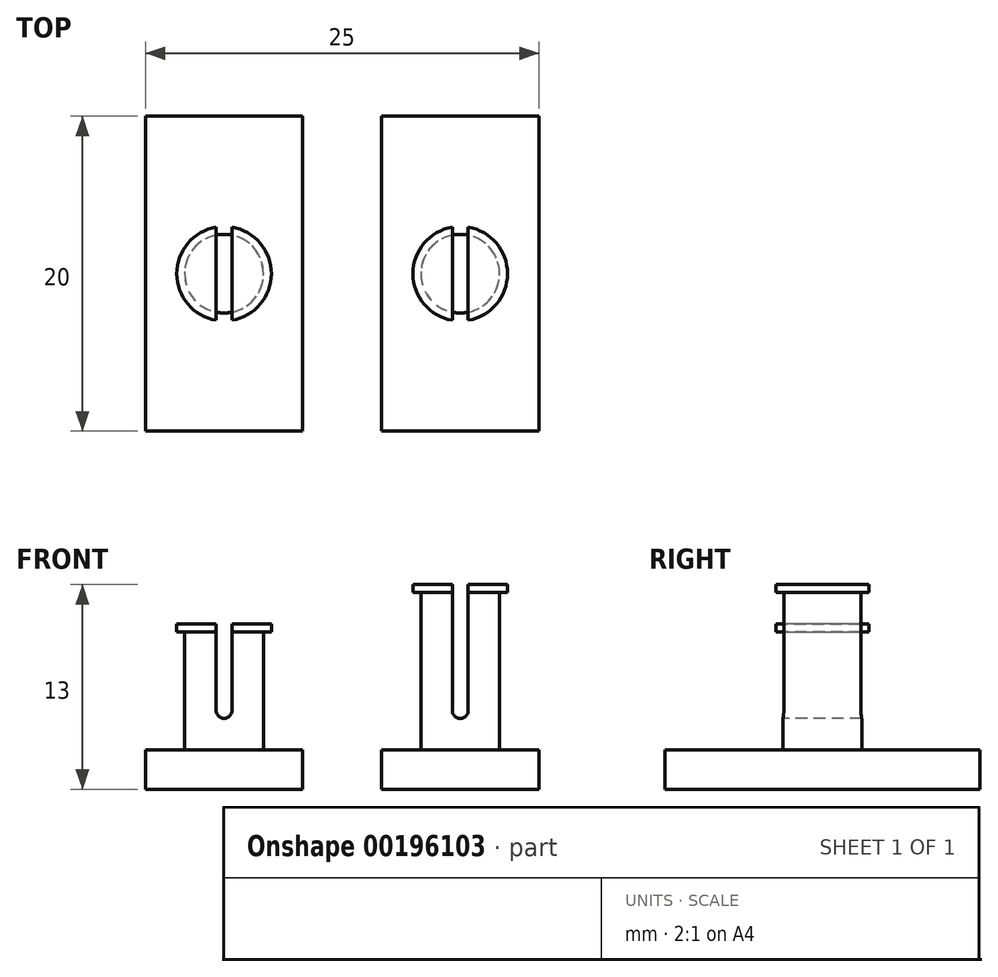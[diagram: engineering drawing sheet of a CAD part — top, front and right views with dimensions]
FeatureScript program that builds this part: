
annotation { "Feature Type Name" : "Feature", "Feature Type Description" : "" }
export const myFeature = defineFeature(function(context is Context, id is Id, definition is map)
    precondition{}
    {
        {
            var Q0;
            Q0=qCreatedBy(makeId("Front.planeOp"),FACE);
            var sketch = newSketch(context, id + "F0", { "sketchPlane" : qUnion([Q0])});
            skLineSegment(sketch, "E0", {"start": v(0, 0) * mm, "end": v(0, 16.22) * mm, "construction": true});
            skLineSegment(sketch, "E1", {"start": v(0, 8) * mm, "end": v(3, 8) * mm});
            skLineSegment(sketch, "E2", {"start": v(3, 8) * mm, "end": v(3, 7.5) * mm});
            skLineSegment(sketch, "E3", {"start": v(3, 7.5) * mm, "end": v(2.5, 7.5) * mm});
            skLineSegment(sketch, "E4", {"start": v(2.5, 7.5) * mm, "end": v(2.5, 2.5) * mm});
            skLineSegment(sketch, "E5", {"start": v(2.5, 2.5) * mm, "end": v(5, 2.5) * mm});
            skLineSegment(sketch, "E6", {"start": v(5, 2.5) * mm, "end": v(5, 0) * mm});
            skLineSegment(sketch, "E7", {"start": v(5, 0) * mm, "end": v(0, 0) * mm});
            skLineSegment(sketch, "E8", {"start": v(0, 8) * mm, "end": v(0, 0) * mm});
            skLineSegment(sketch, "E9", {"start": v(15, 0) * mm, "end": v(15, 15.04) * mm, "construction": true});
            skLineSegment(sketch, "E10", {"start": v(15, 10.5) * mm, "end": v(18, 10.5) * mm});
            skLineSegment(sketch, "E11", {"start": v(18, 10.5) * mm, "end": v(18, 10) * mm});
            skLineSegment(sketch, "E12", {"start": v(18, 10) * mm, "end": v(17.5, 10) * mm});
            skLineSegment(sketch, "E13", {"start": v(17.5, 10) * mm, "end": v(17.5, 2.5) * mm});
            skLineSegment(sketch, "E14", {"start": v(17.5, 2.5) * mm, "end": v(20, 2.5) * mm});
            skLineSegment(sketch, "E15", {"start": v(20, 2.5) * mm, "end": v(20, 0) * mm});
            skLineSegment(sketch, "E16", {"start": v(20, 0) * mm, "end": v(15, 0) * mm});
            skLineSegment(sketch, "E17", {"start": v(15, 10.5) * mm, "end": v(15, 0) * mm});
            skLineSegment(sketch, "E18", {"start": v(30, 0) * mm, "end": v(30, 27.9) * mm, "construction": true});
            skLineSegment(sketch, "E19", {"start": v(30, 13) * mm, "end": v(33, 13) * mm});
            skLineSegment(sketch, "E20", {"start": v(33, 13) * mm, "end": v(33, 12.5) * mm});
            skLineSegment(sketch, "E21", {"start": v(33, 12.5) * mm, "end": v(32.5, 12.5) * mm});
            skLineSegment(sketch, "E22", {"start": v(32.5, 12.5) * mm, "end": v(32.5, 2.5) * mm});
            skLineSegment(sketch, "E23", {"start": v(32.5, 2.5) * mm, "end": v(35, 2.5) * mm});
            skLineSegment(sketch, "E24", {"start": v(35, 2.5) * mm, "end": v(35, 0) * mm});
            skLineSegment(sketch, "E25", {"start": v(35, 0) * mm, "end": v(30, 0) * mm});
            skLineSegment(sketch, "E26", {"start": v(30, 13) * mm, "end": v(30, 0) * mm});
            skSolve(sketch);
        }
        {
            var Q0;
            Q0=makeQuery(id+"F0.imprint","IMPRINT",FACE,{"disambiguationData":[TD([[makeQuery(id+"F0.imprint","IMPRINT",EDGE,{"derivedFrom":sQuery(id+"F0.wireOp",EDGE,"E1")}),-1.0]])]});
            var Q1;
            Q1=sQuery(id+"F0.wireOp",EDGE,"E0");
            revolve(context, id + "F1", {"entities" : qUnion([Q0]), "axis" : qUnion([Q1]), "revolveType" : RevolveType.FULL});
        }
        {
            var Q0;
            Q0=makeQuery(id+"F0.imprint","IMPRINT",FACE,{"disambiguationData":[TD([[makeQuery(id+"F0.imprint","IMPRINT",EDGE,{"derivedFrom":sQuery(id+"F0.wireOp",EDGE,"E10")}),-1.0]])]});
            var Q1;
            Q1=sQuery(id+"F0.wireOp",EDGE,"E9");
            revolve(context, id + "F2", {"entities" : qUnion([Q0]), "axis" : qUnion([Q1]), "revolveType" : RevolveType.FULL});
        }
        {
            var Q0;
            Q0=makeQuery(id+"F0.imprint","IMPRINT",FACE,{"disambiguationData":[TD([[makeQuery(id+"F0.imprint","IMPRINT",EDGE,{"derivedFrom":sQuery(id+"F0.wireOp",EDGE,"E19")}),-1.0]])]});
            var Q1;
            Q1=sQuery(id+"F0.wireOp",EDGE,"E18");
            revolve(context, id + "F3", {"entities" : qUnion([Q0]), "axis" : qUnion([Q1]), "revolveType" : RevolveType.FULL});
        }
        {
            var Q0;
            Q0=qCreatedBy(makeId("Front.planeOp"),FACE);
            var sketch = newSketch(context, id + "F4", { "sketchPlane" : qUnion([Q0])});
            skLineSegment(sketch, "E27", {"start": v(0, 15.96) * mm, "end": v(0, 0) * mm, "construction": true});
            skLineSegment(sketch, "E28", {"start": v(0, 8) * mm, "end": v(0.5, 8) * mm});
            skLineSegment(sketch, "E29", {"start": v(0.5, 8) * mm, "end": v(0.5, 5) * mm});
            skLineSegment(sketch, "E30", {"start": v(0.5, 5) * mm, "end": v(0, 5) * mm, "construction": true});
            skLineSegment(sketch, "E31", {"start": v(0, 5) * mm, "end": v(0, 8) * mm});
            skArc(sketch, "E32", {"start": v(0, 4.5) * mm, "mid": v(0.35, 4.65) * mm, "end": v(0.5, 5) * mm});
            skLineSegment(sketch, "E33.MirrorCS", {"start": v(0, 8) * mm, "end": v(-0.5, 8) * mm});
            skLineSegment(sketch, "E34.MirrorCS", {"start": v(-0.5, 8) * mm, "end": v(-0.5, 5) * mm});
            skArc(sketch, "E35.MirrorCS", {"start": v(0, 4.5) * mm, "mid": v(-0.35, 4.65) * mm, "end": v(-0.5, 5) * mm});
            skLineSegment(sketch, "E36", {"start": v(15, 23.7) * mm, "end": v(15, 7.74) * mm, "construction": true});
            skLineSegment(sketch, "E37", {"start": v(15, 10.5) * mm, "end": v(15.5, 10.5) * mm});
            skLineSegment(sketch, "E38", {"start": v(15.5, 10.5) * mm, "end": v(15.5, 5) * mm});
            skLineSegment(sketch, "E39", {"start": v(15.5, 5) * mm, "end": v(15, 5) * mm, "construction": true});
            skLineSegment(sketch, "E40", {"start": v(15, 5) * mm, "end": v(15, 10.5) * mm});
            skArc(sketch, "E41", {"start": v(15, 4.5) * mm, "mid": v(15.35, 4.65) * mm, "end": v(15.5, 5) * mm});
            skLineSegment(sketch, "E42.MirrorCS", {"start": v(15, 10.5) * mm, "end": v(14.5, 10.5) * mm});
            skLineSegment(sketch, "E43.MirrorCS", {"start": v(14.5, 10.5) * mm, "end": v(14.5, 5) * mm});
            skArc(sketch, "E44.MirrorCS", {"start": v(15, 4.5) * mm, "mid": v(14.65, 4.65) * mm, "end": v(14.5, 5) * mm});
            skLineSegment(sketch, "E45", {"start": v(30, 24.52) * mm, "end": v(30, 8.56) * mm, "construction": true});
            skLineSegment(sketch, "E46", {"start": v(30, 13) * mm, "end": v(30.5, 13) * mm});
            skLineSegment(sketch, "E47", {"start": v(30.5, 13) * mm, "end": v(30.5, 5) * mm});
            skLineSegment(sketch, "E48", {"start": v(30.5, 5) * mm, "end": v(30, 5) * mm, "construction": true});
            skLineSegment(sketch, "E49", {"start": v(30, 5) * mm, "end": v(30, 13) * mm});
            skArc(sketch, "E50", {"start": v(30, 4.5) * mm, "mid": v(30.35, 4.65) * mm, "end": v(30.5, 5) * mm});
            skLineSegment(sketch, "E51.MirrorCS", {"start": v(30, 13) * mm, "end": v(29.5, 13) * mm});
            skLineSegment(sketch, "E52.MirrorCS", {"start": v(29.5, 13) * mm, "end": v(29.5, 5) * mm});
            skArc(sketch, "E53.MirrorCS", {"start": v(30, 4.5) * mm, "mid": v(29.65, 4.65) * mm, "end": v(29.5, 5) * mm});
            skSolve(sketch);
        }
        {
            var Q0;
            Q0=qSketchRegion(id+"F4",true);
            extrude(context, id + "F5", {"entities" : qUnion([Q0]), "operationType" : NewBodyOperationType.REMOVE, "oppositeDirection" : true, "depth" : 25 * mm, "hasSecondDirection" : true, "secondDirectionOppositeDirection" : false, "secondDirectionDepth" : 25 * mm});
        }
        {
            var Q0;
            Q0=makeQuery(id+"F1.opRevolve","SWEPT_FACE",FACE,{"disambiguationData":[OSD([sQuery(id+"F0.wireOp",EDGE,"E7")])]});
            var sketch = newSketch(context, id + "F6", { "sketchPlane" : qUnion([Q0])});
            skLineSegment(sketch, "E54.bottom", {"start": v(-5, 5) * mm, "end": v(5, 5) * mm});
            skLineSegment(sketch, "E54.top", {"start": v(-5, -5) * mm, "end": v(5, -5) * mm});
            skLineSegment(sketch, "E54.left", {"start": v(-5, 5) * mm, "end": v(-5, -5) * mm});
            skLineSegment(sketch, "E54.right", {"start": v(5, 5) * mm, "end": v(5, -5) * mm});
            skLineSegment(sketch, "E55.bottom", {"start": v(10, 10) * mm, "end": v(20, 10) * mm});
            skLineSegment(sketch, "E55.top", {"start": v(10, -10) * mm, "end": v(20, -10) * mm});
            skLineSegment(sketch, "E55.left", {"start": v(10, 10) * mm, "end": v(10, -10) * mm});
            skLineSegment(sketch, "E55.right", {"start": v(20, 10) * mm, "end": v(20, -10) * mm});
            skLineSegment(sketch, "E56.bottom", {"start": v(25, 10) * mm, "end": v(35, 10) * mm});
            skLineSegment(sketch, "E56.top", {"start": v(25, -10) * mm, "end": v(35, -10) * mm});
            skLineSegment(sketch, "E56.left", {"start": v(25, 10) * mm, "end": v(25, -10) * mm});
            skLineSegment(sketch, "E56.right", {"start": v(35, 10) * mm, "end": v(35, -10) * mm});
            skSolve(sketch);
        }
        {
            var Q0;
            Q0=qSketchRegion(id+"F6",true);
            var Q1;
            Q1=makeQuery(id+"F1.opRevolve","SWEPT_FACE",FACE,{"disambiguationData":[OSD([sQuery(id+"F0.wireOp",EDGE,"E5")])]});
            extrude(context, id + "F7", {"entities" : qUnion([Q0]), "operationType" : NewBodyOperationType.ADD, "endBound" : BoundingType.UP_TO_SURFACE, "oppositeDirection" : true, "endBoundEntityFace" : qUnion([Q1]), "depth" : 25 * mm});
        }
        {
            var Q0;
            Q0=makeQuery(id+"F1.opRevolve","SWEPT_BODY",BODY,{"disambiguationData":[OSD([sQuery(id+"F0.wireOp",EDGE,"E1"),sQuery(id+"F0.wireOp",EDGE,"E2"),sQuery(id+"F0.wireOp",EDGE,"E3"),sQuery(id+"F0.wireOp",EDGE,"E4"),sQuery(id+"F0.wireOp",EDGE,"E5"),sQuery(id+"F0.wireOp",EDGE,"E6"),sQuery(id+"F0.wireOp",EDGE,"E7"),sQuery(id+"F0.wireOp",EDGE,"E8")])]});
            deleteBodies(context, id + "F8", {"entities" : qUnion([Q0])});
        }
    });
